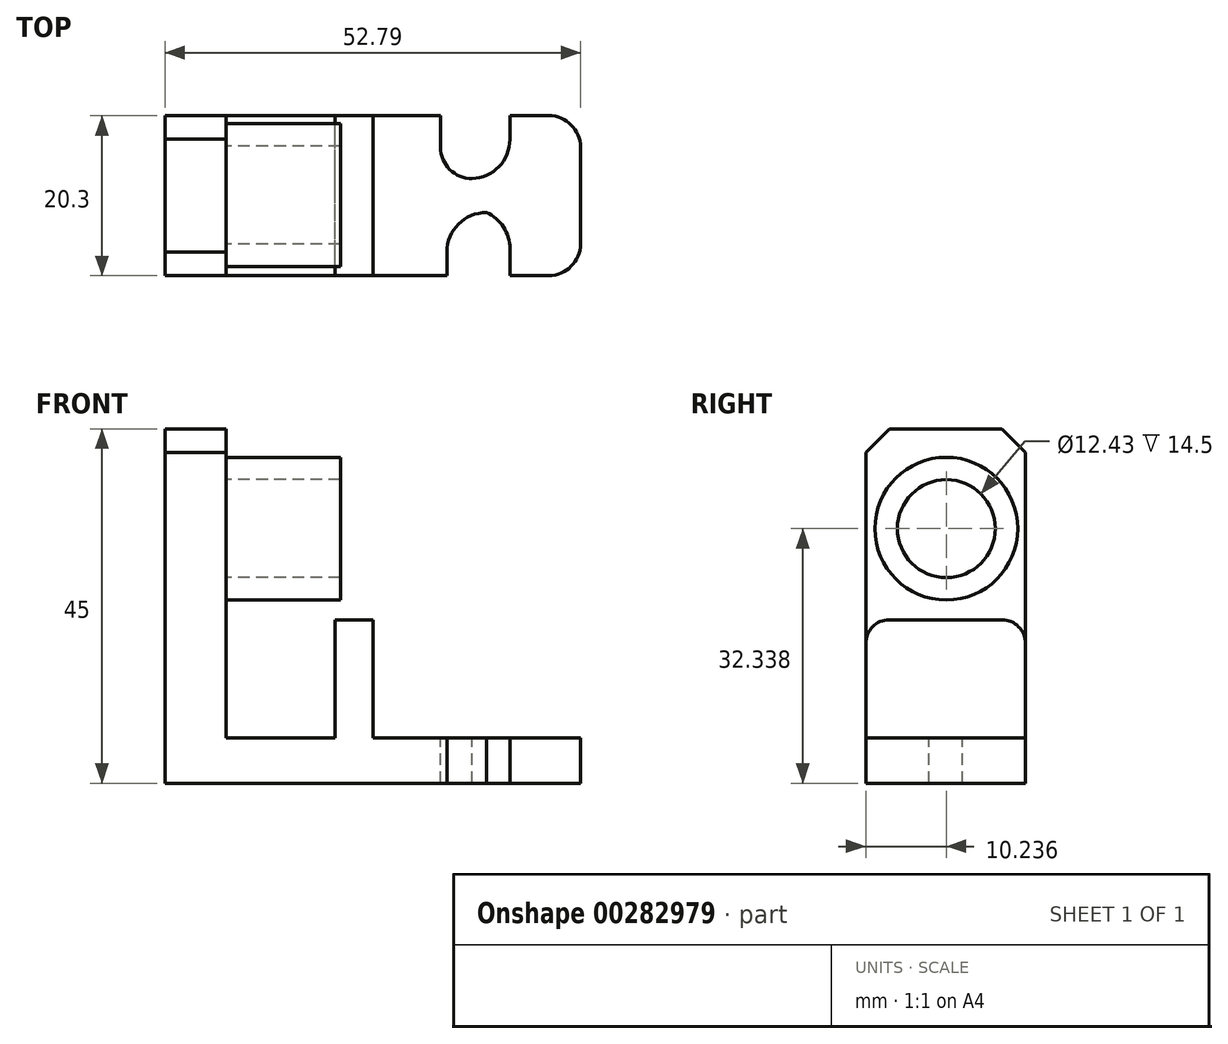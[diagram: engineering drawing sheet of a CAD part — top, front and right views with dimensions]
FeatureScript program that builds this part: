
annotation { "Feature Type Name" : "Feature", "Feature Type Description" : "" }
export const myFeature = defineFeature(function(context is Context, id is Id, definition is map)
    precondition{}
    {
        {
            var Q0;
            Q0=qCreatedBy(makeId("Top.planeOp"),FACE);
            var sketch = newSketch(context, id + "F0", { "sketchPlane" : qUnion([Q0])});
            skLineSegment(sketch, "E0.bottom", {"start": v(-53.88, -20.3) * mm, "end": v(-46.1, -20.3) * mm});
            skLineSegment(sketch, "E0.top", {"start": v(-53.88, 0) * mm, "end": v(-46.1, 0) * mm});
            skLineSegment(sketch, "E0.left", {"start": v(-53.88, -20.3) * mm, "end": v(-53.88, 0) * mm});
            skLineSegment(sketch, "E0.right", {"start": v(-46.1, -20.3) * mm, "end": v(-46.1, 0) * mm});
            skSolve(sketch);
        }
        {
            var Q0;
            Q0 = qSketchRegion(id + "F0", true);
            extrude(context, id + "F1", {"entities" : qUnion([Q0]), "depth" : 45 * mm});
        }
        {
            var Q0;
            Q0=makeQuery(id+"F1.opExtrude","CAP_EDGE",EDGE,{"disambiguationData":[OSD([sQuery(id+"F0.wireOp",EDGE,"E0.bottom")])],"isStart":false});
            var Q1;
            Q1=makeQuery(id+"F1.opExtrude","CAP_EDGE",EDGE,{"disambiguationData":[OSD([sQuery(id+"F0.wireOp",EDGE,"E0.top")])],"isStart":false});
            chamfer(context, id + "F2", {"entities" : qUnion([Q0, Q1]), "width" : 3 * mm, "tangentPropagation" : true});
        }
        {
            var Q0;
            Q0=makeQuery(id+"F1.opExtrude","SWEPT_FACE",FACE,{"disambiguationData":[OSD([sQuery(id+"F0.wireOp",EDGE,"E0.right")])]});
            var sketch = newSketch(context, id + "F3", { "sketchPlane" : qUnion([Q0])});
            skCircle(sketch, "E1", {"center": v(-10.06, 32.34) * mm, "radius": 9.07 * mm});
            skCircle(sketch, "E2", {"center": v(-10.06, 32.34) * mm, "radius": 6.22 * mm});
            skSolve(sketch);
        }
        {
            var Q0;
            {var subQ1=sQuery(id+"F0.wireOp",EDGE,"E0.right");var subQ3=sQuery(id+"F0.wireOp",EDGE,"E0.bottom");Q0=makeQuery(id+"FGDRUUr3F4tPWxM_1.boolean.opBoolean","SPLIT",FACE,{"disambiguationData":[TD([makeQuery(id+"F1.opExtrude","SWEPT_FACE",FACE,{"disambiguationData":[OSD([subQ3])]})])],"derivedFrom":makeQuery(id+"F1.opExtrude","SWEPT_FACE",FACE,{"disambiguationData":[OSD([subQ1])]})});}
            var sketch = newSketch(context, id + "F4", { "sketchPlane" : qUnion([Q0])});
            skLineSegment(sketch, "E3.bottom", {"start": v(-20.3, 0) * mm, "end": v(0, 0) * mm});
            skLineSegment(sketch, "E3.top", {"start": v(-20.3, 5.76) * mm, "end": v(0, 5.76) * mm});
            skLineSegment(sketch, "E3.left", {"start": v(-20.3, 0) * mm, "end": v(-20.3, 5.76) * mm});
            skLineSegment(sketch, "E3.right", {"start": v(0, 0) * mm, "end": v(0, 5.76) * mm});
            skSolve(sketch);
        }
        {
            var Q0;
            Q0 = qSketchRegion(id + "F4", true);
            extrude(context, id + "F5", {"entities" : qUnion([Q0]), "operationType" : NewBodyOperationType.ADD, "depth" : 45 * mm});
        }
        {
            var Q0;
            Q0=makeQuery(id+"F5.opExtrude","SWEPT_FACE",FACE,{"disambiguationData":[OSD([sQuery(id+"F4.wireOp",EDGE,"E3.top")])]});
            var sketch = newSketch(context, id + "F6", { "sketchPlane" : qUnion([Q0])});
            skLineSegment(sketch, "E4.bottom", {"start": v(-27.46, -20.3) * mm, "end": v(-32.3, -20.3) * mm});
            skLineSegment(sketch, "E4.top", {"start": v(-27.46, 0) * mm, "end": v(-32.3, 0) * mm});
            skLineSegment(sketch, "E4.left", {"start": v(-27.46, -20.3) * mm, "end": v(-27.46, 0) * mm});
            skLineSegment(sketch, "E4.right", {"start": v(-32.3, -20.3) * mm, "end": v(-32.3, 0) * mm});
            skSolve(sketch);
        }
        {
            var Q0;
            Q0 = qSketchRegion(id + "F6", true);
            extrude(context, id + "F7", {"entities" : qUnion([Q0]), "operationType" : NewBodyOperationType.ADD, "depth" : 15 * mm});
        }
        {
            var Q0;
            Q0=makeQuery(id+"F7.opExtrude","CAP_EDGE",EDGE,{"disambiguationData":[OSD([sQuery(id+"F6.wireOp",EDGE,"E4.top")])],"isStart":false});
            var Q1;
            Q1=makeQuery(id+"F7.opExtrude","CAP_EDGE",EDGE,{"disambiguationData":[OSD([sQuery(id+"F6.wireOp",EDGE,"E4.bottom")])],"isStart":false});
            fillet(context, id + "F8", {"entities" : qUnion([Q0, Q1]), "radius" : 3 * mm, "tangentPropagation" : true, "allowEdgeOverflow" : false});
        }
        {
            var Q0;
            Q0=makeQuery(id+"F5.opExtrude","CAP_EDGE",EDGE,{"disambiguationData":[OSD([sQuery(id+"F4.wireOp",EDGE,"E3.left")])],"isStart":false});
            var Q1;
            Q1=makeQuery(id+"F5.opExtrude","CAP_EDGE",EDGE,{"disambiguationData":[OSD([sQuery(id+"F4.wireOp",EDGE,"E3.right")])],"isStart":false});
            fillet(context, id + "F9", {"entities" : qUnion([Q0, Q1]), "radius" : 4 * mm, "tangentPropagation" : true, "allowEdgeOverflow" : false});
        }
        {
            var Q0;
            {var subQ2=sQuery(id+"F4.wireOp",EDGE,"E3.top");Q0=makeQuery(id+"F7.boolean.opBoolean","SPLIT",FACE,{"disambiguationData":[TD([makeQuery(id+"F7.opExtrude","SWEPT_FACE",FACE,{"disambiguationData":[OSD([sQuery(id+"F6.wireOp",EDGE,"E4.left")])]})])],"derivedFrom":makeQuery(id+"F5.opExtrude","SWEPT_FACE",FACE,{"disambiguationData":[OSD([subQ2])]})});}
            var sketch = newSketch(context, id + "F10", { "sketchPlane" : qUnion([Q0])});
            skLineSegment(sketch, "E5.bottom", {"start": v(-10.05, -20.3) * mm, "end": v(-18.05, -20.3) * mm});
            skLineSegment(sketch, "E5.top", {"start": v(-10.05, -12.3) * mm, "end": v(-18.05, -12.3) * mm});
            skLineSegment(sketch, "E5.left", {"start": v(-10.05, -20.3) * mm, "end": v(-10.05, -12.3) * mm});
            skLineSegment(sketch, "E5.right", {"start": v(-18.05, -20.3) * mm, "end": v(-18.05, -12.3) * mm});
            skSolve(sketch);
        }
        {
            var Q0;
            Q0 = qSketchRegion(id + "F10", true);
            extrude(context, id + "F11", {"entities" : qUnion([Q0]), "operationType" : NewBodyOperationType.REMOVE, "oppositeDirection" : true, "depth" : 25 * mm});
        }
        {
            var Q0;
            Q0=makeQuery(id+"F11.boolean.opBoolean","COPY",EDGE,{"derivedFrom":makeQuery(id+"F11.opExtrude","SWEPT_EDGE",EDGE,{"disambiguationData":[OSD([sQuery(id+"F10.wireOp",EDGE,"E5.top"),sQuery(id+"F10.wireOp",EDGE,"E5.right")])]})});
            fillet(context, id + "F12", {"entities" : qUnion([Q0]), "radius" : 5 * mm, "tangentPropagation" : true, "allowEdgeOverflow" : false});
        }
        {
            var Q0;
            Q0=makeQuery(id+"F11.boolean.opBoolean","COPY",EDGE,{"derivedFrom":makeQuery(id+"F11.opExtrude","SWEPT_EDGE",EDGE,{"disambiguationData":[OSD([sQuery(id+"F10.wireOp",EDGE,"E5.top"),sQuery(id+"F10.wireOp",EDGE,"E5.left")])]})});
            fillet(context, id + "F13", {"entities" : qUnion([Q0]), "radius" : 5 * mm, "tangentPropagation" : true, "allowEdgeOverflow" : false});
        }
        {
            var Q0;
            {var subQ2=sQuery(id+"F4.wireOp",EDGE,"E3.top");Q0=makeQuery(id+"F7.boolean.opBoolean","SPLIT",FACE,{"disambiguationData":[TD([makeQuery(id+"F7.opExtrude","SWEPT_FACE",FACE,{"disambiguationData":[OSD([sQuery(id+"F6.wireOp",EDGE,"E4.left")])]})])],"derivedFrom":makeQuery(id+"F5.opExtrude","SWEPT_FACE",FACE,{"disambiguationData":[OSD([subQ2])]})});}
            var sketch = newSketch(context, id + "F14", { "sketchPlane" : qUnion([Q0])});
            skPoint(sketch, "E6.firstSnap0", {"position": v(-10.86, -14.15) * mm});
            skLineSegment(sketch, "E6.bottom", {"start": v(-10.86, 0) * mm, "end": v(-18.86, 0) * mm});
            skLineSegment(sketch, "E6.top", {"start": v(-10.86, 0) * mm, "end": v(-18.86, 0) * mm});
            skLineSegment(sketch, "E6.left", {"start": v(-10.86, 0) * mm, "end": v(-10.86, 0) * mm});
            skLineSegment(sketch, "E6.right", {"start": v(-18.86, 0) * mm, "end": v(-18.86, 0) * mm});
            skLineSegment(sketch, "E7.bottom", {"start": v(-18.86, 0) * mm, "end": v(-10.05, 0) * mm});
            skLineSegment(sketch, "E7.top", {"start": v(-18.86, -8) * mm, "end": v(-10.05, -8) * mm});
            skLineSegment(sketch, "E7.left", {"start": v(-18.86, 0) * mm, "end": v(-18.86, -8) * mm});
            skLineSegment(sketch, "E7.right", {"start": v(-10.05, 0) * mm, "end": v(-10.05, -8) * mm});
            skSolve(sketch);
        }
        {
            var Q0;
            Q0 = qSketchRegion(id + "F14", true);
            extrude(context, id + "F15", {"entities" : qUnion([Q0]), "operationType" : NewBodyOperationType.REMOVE, "oppositeDirection" : true, "depth" : 25 * mm});
        }
        {
            var Q0;
            Q0=makeQuery(id+"F15.boolean.opBoolean","COPY",EDGE,{"derivedFrom":makeQuery(id+"F15.opExtrude","SWEPT_EDGE",EDGE,{"disambiguationData":[OSD([sQuery(id+"F14.wireOp",EDGE,"E7.top"),sQuery(id+"F14.wireOp",EDGE,"E7.left")])]})});
            fillet(context, id + "F16", {"entities" : qUnion([Q0]), "radius" : 4 * mm, "tangentPropagation" : true, "allowEdgeOverflow" : false});
        }
        {
            var Q0;
            Q0=makeQuery(id+"F15.boolean.opBoolean","COPY",EDGE,{"derivedFrom":makeQuery(id+"F15.opExtrude","SWEPT_EDGE",EDGE,{"disambiguationData":[OSD([sQuery(id+"F14.wireOp",EDGE,"E7.top"),sQuery(id+"F14.wireOp",EDGE,"E7.right")])]})});
            fillet(context, id + "F17", {"entities" : qUnion([Q0]), "radius" : 5 * mm, "tangentPropagation" : true, "allowEdgeOverflow" : false});
        }
        {
            var Q0;
            Q0=makeQuery(id+"F3.imprint","IMPRINT",FACE,{"disambiguationData":[TD([[makeQuery(id+"F3.imprint","IMPRINT",EDGE,{"derivedFrom":sQuery(id+"F3.wireOp",EDGE,"E1")}),1.0]])]});
            extrude(context, id + "F18", {"entities" : qUnion([Q0]), "operationType" : NewBodyOperationType.ADD, "depth" : 14.5 * mm});
        }
    });
